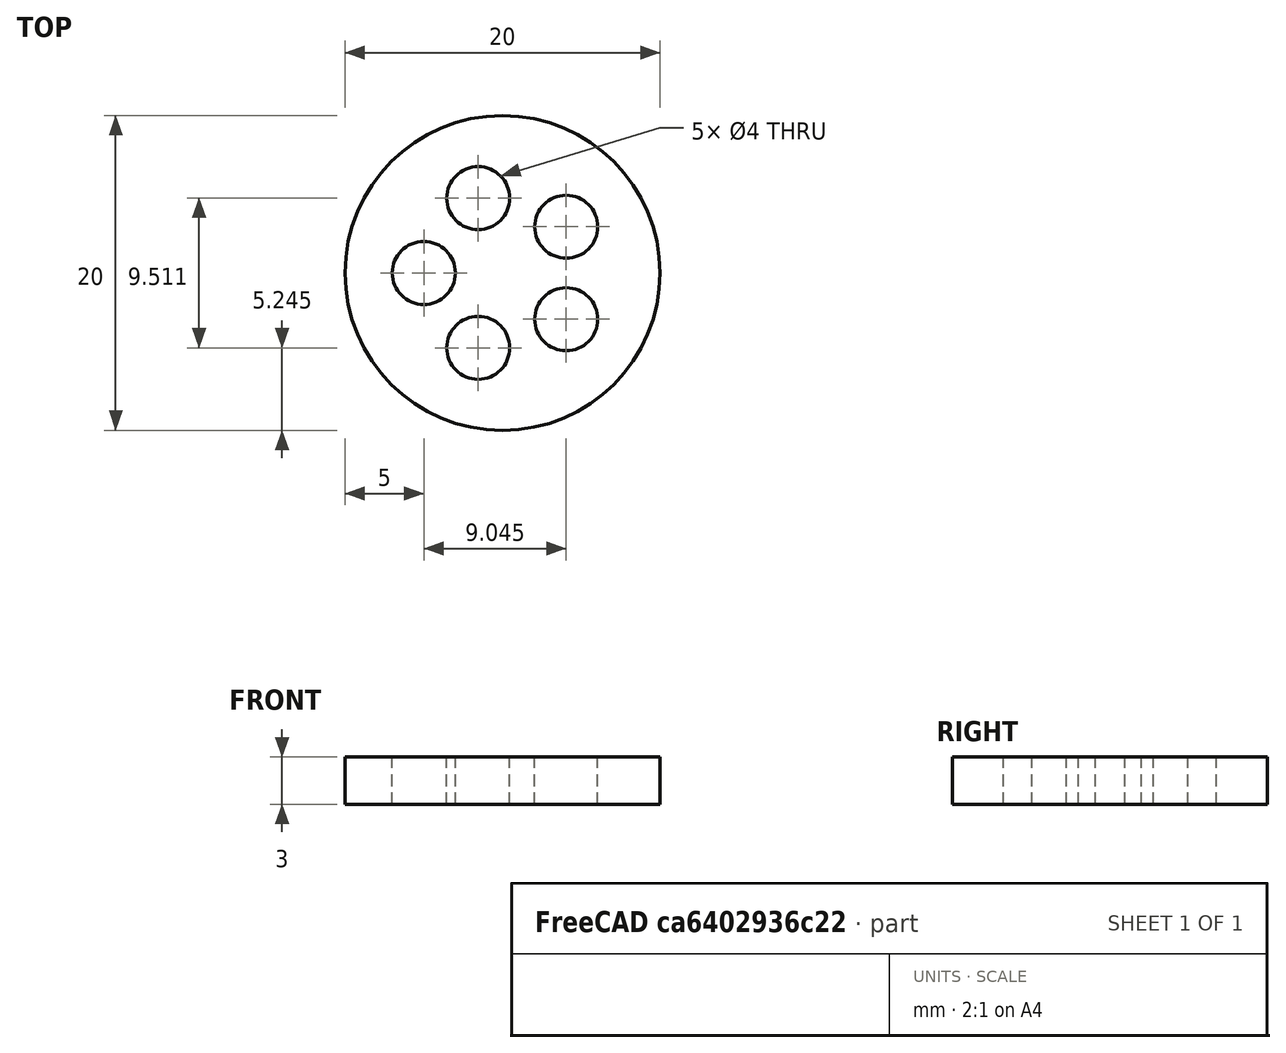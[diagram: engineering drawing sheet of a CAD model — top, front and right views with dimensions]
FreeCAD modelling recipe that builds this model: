
FCSTD DOCUMENT  (FreeCAD 0.16R6707 (Git))
Label: 05-pieza-mecano-polar
License: All rights reserved
LicenseURL: http://en.wikipedia.org/wiki/All_rights_reserved
objects: Part::Cylinder×2, Part::FeaturePython×1, Part::Cut×1
note: 4 computed .brp shape members not serialized (recipe doc carries the construction recipe); baked Part::Feature solids carry a one-line shape summary decoded from their .brp

FEATURE [Part::Cylinder] Cylinder  label="Cilindro"
  Angle = 360
  Height = 3
  Radius = 10
FEATURE [Part::Cylinder] Cylinder001  label="Cilindro001"
  Angle = 360
  Height = 10
  Placement = pos=(-5,0,-5) rot=(0,0,1;0rad)
  Radius = 2
FEATURE [Part::FeaturePython] Array  # Draft array (typed FeaturePython)
  Angle = 360
  ArrayType = 1
  Axis = (0,0,1)
  Base = -> Cylinder001
  Center = (0,0,0)
  Fuse = false
  IntervalAxis = (0,0,0)
  IntervalX = (1,0,0)
  IntervalY = (0,1,0)
  IntervalZ = (0,0,0)
  NumberPolar = 5
  NumberX = 2
  NumberY = 2
  NumberZ = 1
FEATURE [Part::Cut] Cut
  Base = -> Cylinder
  Tool = -> Array
